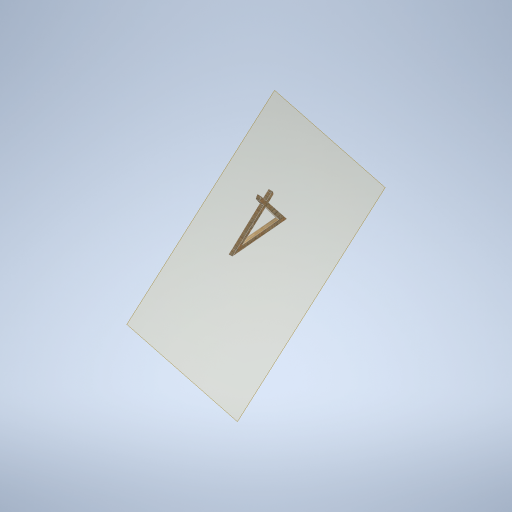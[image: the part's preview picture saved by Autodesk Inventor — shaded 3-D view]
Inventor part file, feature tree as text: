
AUTODESK INVENTOR PART (.ipt)
format: ipt  version: 2024.2 (Build 282272000, 272)  size: 501,760 bytes
history: native  units: mm
features: sketch x10, plane x6, extrude x4, projected_geometry x3, loft x2, other x1
ambient origin geometry x8: Origin, YZ Plane, XZ Plane, XY Plane, X Axis, Y Axis, Z Axis, Center Point
bodies: Solid1 (feature_tree)
feature tree (26):
  sketch  "Sketch1"  dims[d5=0.0mm d6=-8101.0mm d7=800.0mm]
  plane  "Work Plane2"
  loft  "Loft1"
  plane  "Work Plane3"
  extrude  "Extrusion1"  TaperAngle=0.0deg  [1 undecoded]
  sketch  "Sketch5"  dims[d15=6.981317mm d16=0.0mm d17=0.0mm]
  plane  "Work Plane4"
  extrude  "Extrusion2"  TaperAngle=0.0deg  [1 undecoded]
  plane  "Work Plane5"
  sketch  "Sketch7"  dims[d21=0.0mm d22=90.0deg d23=0.0mm d24=0.0mm]
  sketch  "Sketch8"  dims[d28=150.0mm d29=0.0mm]
  loft  "Loft2"
  sketch  "Sketch9"
  plane  "Work Plane6"
  extrude  "Extrusion3"  TaperAngle=0.0deg  [1 undecoded]
  extrude  "Extrusion4"  TaperAngle=0.0deg  [1 undecoded]
  plane  "Work Plane1"
  sketch  "Sketch2"  dims[d8=0.0mm d9=90.0deg d10=0.0mm d11=90.0deg]
  sketch  "Sketch3"  dims[d12=2600.0mm d13=0.0mm d14=0.0mm]
  sketch  "Sketch6"  dims[d18=90.0deg d19=0.0mm d20=90.0deg]
  projected_geometry  "Projected Loop1"
  projected_geometry  "Projected Loop2"
  other  "Edges1"
  projected_geometry  "Projected Loop3"
  sketch  "Sketch10"
  sketch  "Sketch11"
note: 4 required parameter values undecoded (feature->parameter linkage not recoverable at this tier; creation-order binding heuristic only, values carry confidence <= 0.55)
